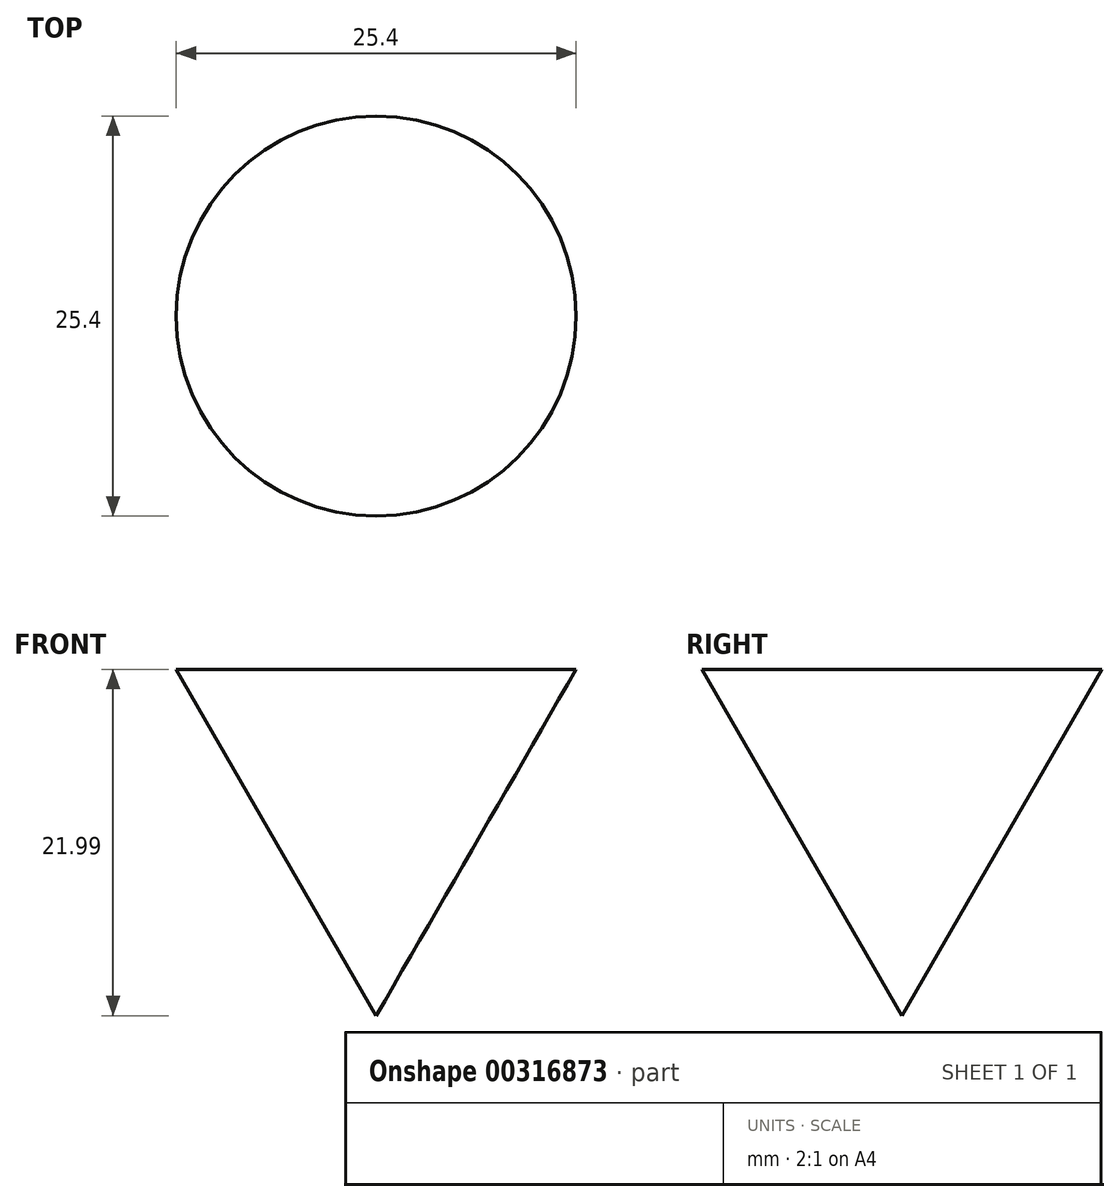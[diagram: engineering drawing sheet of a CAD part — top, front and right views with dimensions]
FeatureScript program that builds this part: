
annotation { "Feature Type Name" : "Feature", "Feature Type Description" : "" }
export const myFeature = defineFeature(function(context is Context, id is Id, definition is map)
    precondition{}
    {
        {
            var Q0;
            Q0=qCreatedBy(makeId("Front.planeOp"),FACE);
            var sketch = newSketch(context, id + "F0", { "sketchPlane" : qUnion([Q0])});
            skCircle(sketch, "E0.cCircle", {"center": v(0, 0) * mm, "radius": 7.33 * mm, "construction": true});
            skLineSegment(sketch, "E0.0", {"start": v(-12.7, 7.33) * mm, "end": v(12.7, 7.33) * mm});
            skLineSegment(sketch, "E0.1", {"start": v(12.7, 7.33) * mm, "end": v(0, -14.66) * mm});
            skLineSegment(sketch, "E0.2", {"start": v(0, -14.66) * mm, "end": v(-12.7, 7.33) * mm});
            skPoint(sketch, "E0.0.midPoint", {"position": v(0, 7.33) * mm});
            skLineSegment(sketch, "E1", {"start": v(0, -14.66) * mm, "end": v(0, 7.33) * mm});
            skSolve(sketch);
        }
        {
            var Q0;
            {var subQ0=sQuery(id+"F0.wireOp",EDGE,"E0.2");Q0=makeQuery(id+"F0.imprint","IMPRINT",FACE,{"disambiguationData":[TD([[makeQuery(id+"F0.imprint","IMPRINT",EDGE,{"derivedFrom":subQ0}),-1.0]])]});}
            var Q1;
            Q1=sQuery(id+"F0.wireOp",EDGE,"E1");
            revolve(context, id + "F1", {"entities" : qUnion([Q0]), "axis" : qUnion([Q1]), "revolveType" : RevolveType.FULL});
        }
    });
